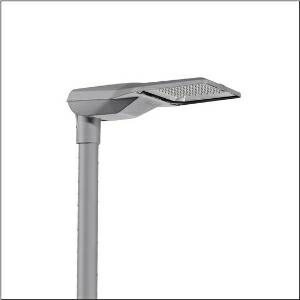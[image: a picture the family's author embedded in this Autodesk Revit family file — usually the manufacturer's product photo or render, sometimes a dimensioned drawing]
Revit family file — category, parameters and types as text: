
# Revit family: streetlight_sl_21_iq_midi___p0_5a_5xe3v31d08mb_1276
name_source: partatom
category: Lighting Fixtures
units: mm (PartAtom-declared; Revit-internal decimal feet)

## family parameters
Cut with Voids When Loaded = No
Host = Face
Light Source = No
Part Type = Normal
Room Calculation Point = No
Round Connector Dimension = Use Diameter
Shared = No

## types (1)
- --- (1 x LED, 19170 lm, 146.7 W, 3000K)
    Apparent Load = 147 VA
    CIE Flux Codes = 37 73 96 100 100
    Color Rendering = 70
    Color Temperature = 3000K
    Default Elevation = 1800 mm
    Description = Streetlight SL 21 iQ midi, mast luminaire, primary light control with lens, of PMMA, primary optical cover: cover, of toughened safety glass, transparent, light distribution: P0.5a, light emission: direct distribution, primary light characteristic: asymmetric, installation type: post-top, side-entry, LED, High Power LED, rated luminous flux: 19.170lm, luminous efficacy: 131lm/W, light colour: 730, colour temperature: 3000K, control gear: iQ-Comfort, control: pre-setting: linear dimming characteristic, Auto-Match, Temp-Guard, Lumen-Switch, Night-Set, Smart-Wire, Light-Fading, Desk-Remote (wireless, voltage-free reading and setting of iQ features in the workshop via application-optimized NFC function/RFID function), optimised constant luminous flux control (CLO 2.0), mains connection: 230..240V, AC, 50/60Hz, start of lifetime: 147W, end of service life: 161W, reduction: 62W, luminaire housing, of diecast aluminium, powder-coated, Siteco® metallic grey (DB 702S), corrosivity category C5 mid according to DIN EN ISO 12944, please order mast flange separately, inclination adjustable: 0°, 5°, 10°, 15°, sealing non-destructively replaceable, multi-level sealing system, length: 644mm, width: 335mm, height: 110mm, mast flange for spigot size: 42mm (side-entry): 5XC10008XM4, 60/48mm (side-entry/post-top): 5XC10108XM2, 76/60mm (side-entry/post-top): 5XC10108XM1, mounting height: 4..8m, protection rating (complete): IP66, insulation class (complete): insulation class II (safety insulation), certification: CE, ENEC, ENEC+, VDE, impact resistance: IK10, permissible operating ambient temperature for outdoor applications: -40..+50°C, standard-compliant lighting for roads and squares, packaging unit: 1 piece

Light Distribution: P0.5a
    Height = 111 mm
    Lamp = 1 x LED
    Lamp Light Flux = 19170 lm
    Lamp Power = 146.7 W
    Lamp count = 1
    Length = 644 mm
    Luminous efficacy = 131 lm/W
    Manufacturer = Siteco
    ModVariant = No
    Model = 5XE3V31D08MB
    Number of Poles = 1
    OnlyDefault = Yes
    Power Factor = 1
    Product Name = Streetlight SL 21 iQ midi | P0.5a
    Product group = mast luminaire | pylon top
    ProductGroupID = 6100
    Protection Class = Protection class II
    Protection Degree = IP 66
    RLX_Detail_Level = 1
    RLX_Emergency_Light_Flux = 0 lm
    RLX_Emergency_Type = 0
    RLX_Emergency_Type_DB = No
    RlxData = <blob elided: 26473 chars, md5=caceada7>
    Socket = socket
    Standby Power = 0 W
    System Light Flux = 19169 lm
    System Power = 147 W
    Type Comments = factory setting: luminous flux: 100 % | dim-lin: 254 | 753 mA
    Type Image = l_1004298.jpg
    URL = http://relux.com
    VarID = @adj_069654
    Voltage = 0 V
    Weight = 0.00 kg
    Width = 336 mm

## geometry (parser evidence)
native form markers: Blend x4, Sweep x13
no freeform markers — native parametric forms only
